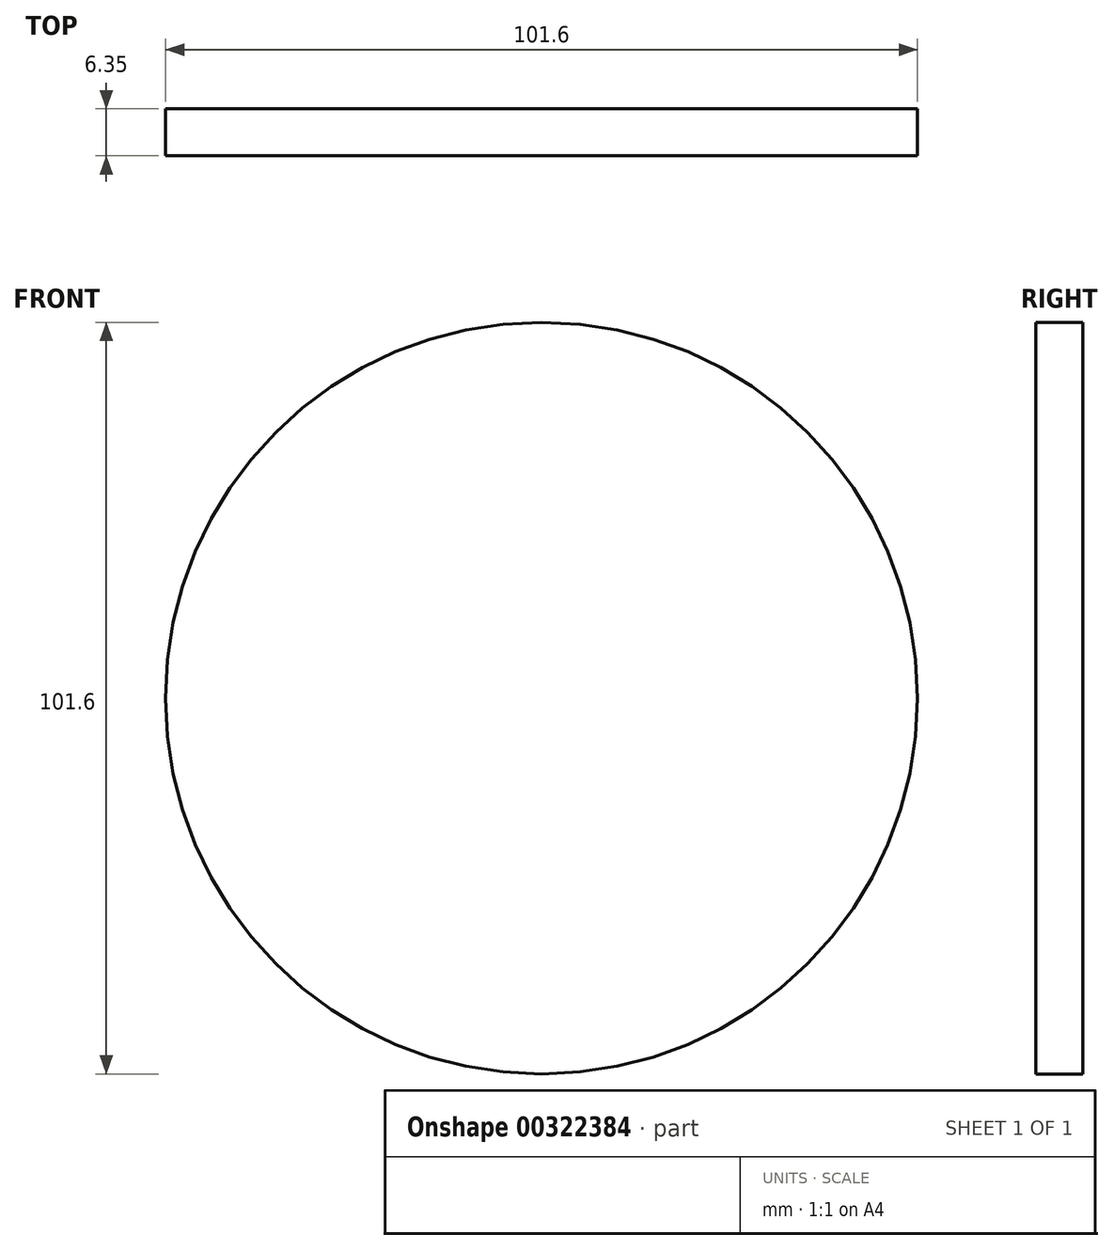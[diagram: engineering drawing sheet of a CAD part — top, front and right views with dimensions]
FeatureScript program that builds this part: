
annotation { "Feature Type Name" : "Feature", "Feature Type Description" : "" }
export const myFeature = defineFeature(function(context is Context, id is Id, definition is map)
    precondition{}
    {
        {
            var Q0;
            Q0=qCreatedBy(makeId("Front.planeOp"),FACE);
            var sketch = newSketch(context, id + "F0", { "sketchPlane" : qUnion([Q0])});
            skCircle(sketch, "E0", {"center": v(0, 0) * mm, "radius": 50.8 * mm});
            skSolve(sketch);
        }
        {
            var Q0;
            Q0=qSketchRegion(id+"F0",true);
            extrude(context, id + "F1", {"entities" : qUnion([Q0]), "depth" : 6.35 * mm});
        }
    });
